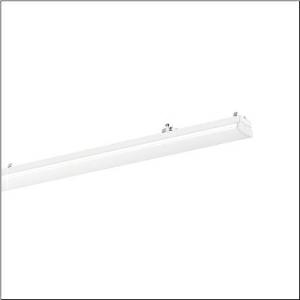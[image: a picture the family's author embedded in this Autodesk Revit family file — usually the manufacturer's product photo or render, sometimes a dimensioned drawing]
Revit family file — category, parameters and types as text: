
# Revit family: licross_r__11_recessed_opal_ho_51tl1ddn4d5m_587a
name_source: partatom
category: Lighting Fixtures
units: mm (PartAtom-declared; Revit-internal decimal feet)

## family parameters
Cut with Voids When Loaded = No
Host = Face
Light Source = No
Part Type = Normal
Room Calculation Point = No
Round Connector Dimension = Use Diameter
Shared = No

## types (1)
- --- (1 x LED, 13620 lm, 76.8 W, 4000K)
    Apparent Load = 77 VA
    CIE Flux Codes = 44 73 91 87 100
    Color Rendering = 80
    Color Temperature = 4000K
    Default Elevation = 1800 mm
    Description = Licross® 11 recessed opal HO, luminaire insert, of sheet steel, coil coated, white, length: 1.500mm, width: 76mm, height: 87mm, LED rated luminous flux: 13.620lm, light colour: 840, control gear: DALI 2, with plug, 5-pole, with phase selection, mains connection: 220..240V, AC, 50/60Hz, rated input power: 77W, halogen-free wiring, primary optical cover: cover, of PMMA, light emission: direct with ceiling illumination distribution, primary light characteristic: symmetric, protection rating (complete): IP40, insulation class (complete): insulation class I (protective earthing), certification: CE, ENEC, VDE, UKCA, protection symbol: D if used in an environment without relevant dust loads with corresponding accessories, impact resistance: IK06, permissible ambient temperature for indoor applications: -25..+30°C, corresponds to IFS (International Featured Standards) requirements for safety and quality in the food industry, reducing of maximum allowable ambient temperature of 5°C with ceiling mounting, LABS conformity tested according to VDMA 24364:2018-05, packaging unit: 1 piece
    Height = 83 mm
    Lamp = 1 x LED
    Lamp Light Flux = 13620 lm
    Lamp Power = 76.8 W
    Lamp count = 1
    Length = 1500 mm
    Luminous efficacy = 177 lm/W
    Manufacturer = Siteco
    ModVariant = No
    Model = 51TL1DDN4D5M
    Mounting Place = Ceiling
    Mounting Type = Pendant
    Number of Poles = 1
    OnlyDefault = Yes
    Power Factor = 1
    Product Name = Licross® 11 recessed opal HO
    Product group = luminaire insert
    ProductGroupID = 902
    Protection Class = Protection class I
    Protection Degree = IP 40
    RLX_Detail_Level = 1
    RLX_Emergency_Light_Flux = 0 lm
    RLX_Emergency_Type = 0
    RLX_Emergency_Type_DB = No
    RlxData = <blob elided: 27353 chars, md5=4a65c32d>
    Socket = socket
    Standby Power = 0 W
    System Light Flux = 13620 lm
    System Power = 77 W
    Type Comments = factory setting: luminous flux: 100 % | dim-lin: 254 | 522 mA
    Type Image = l_1313666.jpg
    URL = http://relux.com
    VarID = @adj_076066
    Voltage = 0 V
    Weight = 0.00 kg
    Width = 76 mm

## geometry (parser evidence)
native form markers: Blend x4, Sweep x13
no freeform markers — native parametric forms only
